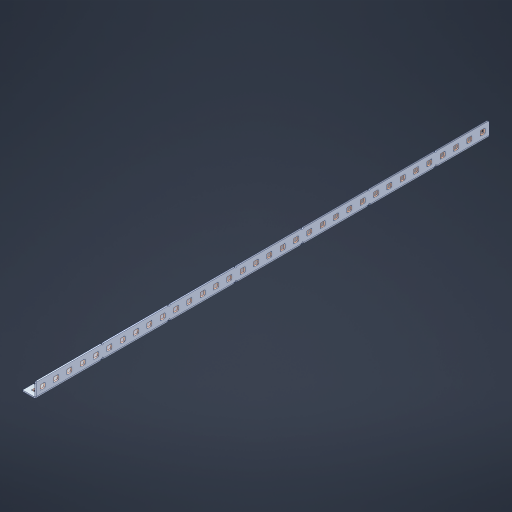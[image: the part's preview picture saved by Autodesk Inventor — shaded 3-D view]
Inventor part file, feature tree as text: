
AUTODESK INVENTOR PART (.ipt)
format: ipt  version: 2023 (Build 270158000, 158)  size: 1,323,520 bytes
history: native  units: in
note: dims shown in document units (in); Inventor stores cm internally (conversion verified against a paired STEP export)
features: other x109, extrude x100, sheet_metal_op x11, sketch x10, pattern_linear x2, mirror x1, chamfer x1
ambient origin geometry x8: Origin, YZ Plane, XZ Plane, XY Plane, X Axis, Y Axis, Z Axis, Center Point
bodies: Solid1 (feature_tree), Body (feature_tree)
feature tree (234):
  sheet_metal_op  "Flanges"
  other  "Flange Pattern Plane"
  other  "Flange Pattern Sketch"
  sheet_metal_op  "Flange Pattern"
  sheet_metal_op  "Body Pattern"
  pattern_linear  "Center Pattern"  Spacing1=0.0469in  [1 undecoded]
  other  "Arc Length"
  mirror  "Notch Mirror"
  pattern_linear  "Notch Pattern"  Spacing1=0.182in  [1 undecoded]
  chamfer  "End Chamfer"
  extrude  "Half Cut"  Depth=0.02in
  sketch  "Sketch1"  dims[d0=1.0in]
  other  "Plate1"
  sketch  "Sketch2"  dims[d1=17.0in]
  other  "Plate2"
  sheet_metal_op  "Bend1"
  sheet_metal_op  "Corner1"
  sketch  "Sketch3"  dims[d2=0.0469in]
  sketch  "Sketch7"  dims[d3=0.0469in]
  other  "Srf1"
  other  "Srf2"
  sketch  "Sketch8"  dims[d4=0.0234in]
  sketch  "Sketch9"  dims[d5=0.0938in]
  other  "Srf91"
  sheet_metal_op  "Body Pattern Sketch"
  other  "Srf92"
  sketch  "Sketch13"  dims[d6=0.0469in]
  sketch  "Sketch14"  dims[d7=0.5in d8=90.0deg d9=0.0312in]
  sketch  "Sketch15"  dims[d10=0.1875in]
  sketch  "Sketch16"  dims[d11=0.0469in d12=0.0469in d16=0.182in d17=0.02in d18=0.0469in d19=0.0in d20=0.25in d21=0.25in d38=13.3858in d40=0.5in d41=0.3937in d43=1.0in d46=0.172in d47=1.0in d48=0.0in d49=0.182in d50=0.02in d51=0.25in d52=0.25in d53=0.0469in d54=0.0in d55=0.172in d56=1.0in d57=0.0in d58=0.25in d60=13.3858in d62=0.5in d63=0.3937in d65=0.5in d85=0.1227in d86=0.1659in d88=0.04in d89=0.0469in d90=0.0in d91=0.04in d92=0.0491in d95=2.5in d96=0.04in d97=0.25in d98=45.0deg d99=0.25in d100=0.5in d101=0.0in d102=2.497in d106=0.182in d107=0.02in d108=0.5in d109=0.5in d110=0.0469in d111=0.0in d112=0.172in d113=0.5in d114=0.0in d117=0.5in d118=0.5in d119=0.5in]
  other  "Srf786"
  other  "Srf823"
  other  "Srf824"
  other  "Srf825"
  other  "Srf826"
  other  "Srf827"
  other  "Srf828"
  other  "Srf829"
  other  "Srf856"
  other  "Srf857"
  other  "Srf858"
  other  "Srf859"
  other  "Srf860"
  other  "Srf861"
  other  "Srf862"
  other  "Srf889"
  other  "Srf890"
  other  "Srf891"
  other  "Srf892"
  other  "Srf893"
  other  "Srf894"
  other  "Srf895"
  other  "Srf896"
  other  "Srf922"
  other  "Srf923"
  other  "Srf924"
  other  "Srf925"
  other  "Srf926"
  other  "Srf959"
  other  "Srf960"
  other  "Srf961"
  other  "Srf962"
  other  "Srf963"
  other  "Srf996"
  other  "Srf997"
  other  "Srf998"
  other  "Srf999"
  other  "Srf1000"
  other  "Srf1143"
  other  "Srf1144"
  other  "Srf1145"
  other  "Srf1146"
  other  "Srf1147"
  other  "Srf1148"
  other  "Srf1149"
  other  "Srf1150"
  other  "Srf1151"
  other  "Srf1152"
  other  "Srf1153"
  other  "Srf1154"
  other  "Srf1155"
  other  "Srf1156"
  other  "Srf1157"
  other  "Srf1158"
  other  "Srf1159"
  other  "Srf1160"
  other  "Srf1161"
  other  "Srf1162"
  other  "Srf1199"
  other  "Srf1200"
  other  "Srf1201"
  other  "Srf1202"
  other  "Srf1203"
  other  "Srf1204"
  other  "Srf1205"
  other  "Srf1206"
  other  "Srf1207"
  other  "Srf1208"
  other  "Srf1209"
  other  "Srf1210"
  other  "Srf1211"
  other  "Srf1212"
  other  "Srf1213"
  other  "Srf1214"
  other  "Srf1215"
  other  "Srf1216"
  other  "Srf1217"
  other  "Srf1218"
  other  "Srf1255"
  other  "Srf1256"
  other  "Srf1257"
  other  "Srf1258"
  other  "Srf1259"
  other  "Srf1260"
  other  "Srf1261"
  other  "Srf1262"
  other  "Srf1263"
  other  "Srf1264"
  other  "Srf1265"
  other  "Srf1266"
  other  "Srf1267"
  other  "Srf1268"
  other  "Srf1269"
  other  "Srf1270"
  other  "Srf1271"
  other  "Srf1272"
  other  "Srf1273"
  other  "Srf1274"
  sheet_metal_op  "Flange Stamp"
  sheet_metal_op  "Flange Circle"
  sheet_metal_op  "Body Stamp"
  sheet_metal_op  "Body Circle"
  other  "Center Stamp"
  other  "Center Circle"
  sheet_metal_op  "Notch"
  extrude  "ExtrusionSrf2"  Depth=0.0469in
  extrude  "ExtrusionSrf92"  TaperAngle=0.0deg  [1 undecoded]
  extrude  "ExtrusionSrf823"  Depth=0.25in
  extrude  "ExtrusionSrf824"  Depth=0.25in
  extrude  "ExtrusionSrf825"  Depth=0.5in
  extrude  "ExtrusionSrf826"  Depth=0.5in
  extrude  "ExtrusionSrf827"  Depth=1.0in TaperAngle=0.0deg
  extrude  "ExtrusionSrf828"  Depth=0.182in
  extrude  "ExtrusionSrf829"  Depth=0.02in
  extrude  "ExtrusionSrf856"  Depth=0.25in
  extrude  "ExtrusionSrf857"  Depth=0.25in
  extrude  "ExtrusionSrf858"  Depth=0.0469in
  extrude  "ExtrusionSrf859"  TaperAngle=0.0deg  [1 undecoded]
  extrude  "ExtrusionSrf860"  Depth=0.5in
  extrude  "ExtrusionSrf861"  Depth=1.0in TaperAngle=0.0deg
  extrude  "ExtrusionSrf862"  Depth=0.25in
  extrude  "ExtrusionSrf889"  Depth=0.5in
  extrude  "ExtrusionSrf890"  Depth=0.5in
  extrude  "ExtrusionSrf891"  Depth=0.5in
  extrude  "ExtrusionSrf892"  Depth=0.5in
  extrude  "ExtrusionSrf893"  Depth=0.5in
  extrude  "ExtrusionSrf894"  Depth=0.0469in
  extrude  "ExtrusionSrf895"  TaperAngle=0.0deg  [1 undecoded]
  extrude  "ExtrusionSrf896"  Depth=0.5in
  extrude  "ExtrusionSrf922"  Depth=0.5in
  extrude  "ExtrusionSrf923"  Depth=2.5in
  extrude  "ExtrusionSrf924"  Depth=0.25in TaperAngle=45.0deg
  extrude  "ExtrusionSrf925"  Depth=0.25in
  extrude  "ExtrusionSrf926"  Depth=0.5in TaperAngle=0.0deg
  extrude  "ExtrusionSrf959"  Depth=0.5in
  extrude  "ExtrusionSrf960"  Depth=0.182in
  extrude  "ExtrusionSrf961"  Depth=0.02in
  extrude  "ExtrusionSrf962"  Depth=0.5in
  extrude  "ExtrusionSrf963"  Depth=0.5in
  extrude  "ExtrusionSrf996"  Depth=0.0469in
  extrude  "ExtrusionSrf997"  TaperAngle=0.0deg  [1 undecoded]
  extrude  "ExtrusionSrf998"  Depth=0.5in
  extrude  "ExtrusionSrf999"  Depth=0.5in TaperAngle=0.0deg
  extrude  "ExtrusionSrf1000"  Depth=0.5in
  extrude  "ExtrusionSrf1143"  Depth=0.5in
  extrude  "ExtrusionSrf1144"  Depth=0.5in
  extrude  "ExtrusionSrf1145"  [1 undecoded]
  extrude  "ExtrusionSrf1146"  [1 undecoded]
  extrude  "ExtrusionSrf1147"  [1 undecoded]
  extrude  "ExtrusionSrf1148"  [1 undecoded]
  extrude  "ExtrusionSrf1149"  [1 undecoded]
  extrude  "ExtrusionSrf1150"  [1 undecoded]
  extrude  "ExtrusionSrf1151"  [1 undecoded]
  extrude  "ExtrusionSrf1152"  [1 undecoded]
  extrude  "ExtrusionSrf1153"  [1 undecoded]
  extrude  "ExtrusionSrf1154"  [1 undecoded]
  extrude  "ExtrusionSrf1155"  [1 undecoded]
  extrude  "ExtrusionSrf1156"  [1 undecoded]
  extrude  "ExtrusionSrf1157"  [1 undecoded]
  extrude  "ExtrusionSrf1158"  [1 undecoded]
  extrude  "ExtrusionSrf1159"  [1 undecoded]
  extrude  "ExtrusionSrf1160"  [1 undecoded]
  extrude  "ExtrusionSrf1161"  [1 undecoded]
  extrude  "ExtrusionSrf1162"  [1 undecoded]
  extrude  "ExtrusionSrf1199"  [1 undecoded]
  extrude  "ExtrusionSrf1200"  [1 undecoded]
  extrude  "ExtrusionSrf1201"  [1 undecoded]
  extrude  "ExtrusionSrf1202"  [1 undecoded]
  extrude  "ExtrusionSrf1203"  [1 undecoded]
  extrude  "ExtrusionSrf1204"  [1 undecoded]
  extrude  "ExtrusionSrf1205"  [1 undecoded]
  extrude  "ExtrusionSrf1206"  [1 undecoded]
  extrude  "ExtrusionSrf1207"  [1 undecoded]
  extrude  "ExtrusionSrf1208"  [1 undecoded]
  extrude  "ExtrusionSrf1209"  [1 undecoded]
  extrude  "ExtrusionSrf1210"  [1 undecoded]
  extrude  "ExtrusionSrf1211"  [1 undecoded]
  extrude  "ExtrusionSrf1212"  [1 undecoded]
  extrude  "ExtrusionSrf1213"  [1 undecoded]
  extrude  "ExtrusionSrf1214"  [1 undecoded]
  extrude  "ExtrusionSrf1215"  [1 undecoded]
  extrude  "ExtrusionSrf1216"  [1 undecoded]
  extrude  "ExtrusionSrf1217"  [1 undecoded]
  extrude  "ExtrusionSrf1218"  [1 undecoded]
  extrude  "ExtrusionSrf1255"  [1 undecoded]
  extrude  "ExtrusionSrf1256"  [1 undecoded]
  extrude  "ExtrusionSrf1257"  [1 undecoded]
  extrude  "ExtrusionSrf1258"  [1 undecoded]
  extrude  "ExtrusionSrf1259"  [1 undecoded]
  extrude  "ExtrusionSrf1260"  [1 undecoded]
  extrude  "ExtrusionSrf1261"  [1 undecoded]
  extrude  "ExtrusionSrf1262"  [1 undecoded]
  extrude  "ExtrusionSrf1263"  [1 undecoded]
  extrude  "ExtrusionSrf1264"  [1 undecoded]
  extrude  "ExtrusionSrf1265"  [1 undecoded]
  extrude  "ExtrusionSrf1266"  [1 undecoded]
  extrude  "ExtrusionSrf1267"  [1 undecoded]
  extrude  "ExtrusionSrf1268"  [1 undecoded]
  extrude  "ExtrusionSrf1269"  [1 undecoded]
  extrude  "ExtrusionSrf1270"  [1 undecoded]
  extrude  "ExtrusionSrf1271"  [1 undecoded]
  extrude  "ExtrusionSrf1272"  [1 undecoded]
  extrude  "ExtrusionSrf1273"  [1 undecoded]
  extrude  "ExtrusionSrf1274"  [1 undecoded]
note: 64 required parameter values undecoded (feature->parameter linkage not recoverable at this tier; creation-order binding heuristic only, values carry confidence <= 0.55)
